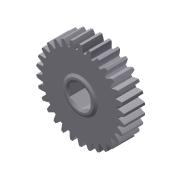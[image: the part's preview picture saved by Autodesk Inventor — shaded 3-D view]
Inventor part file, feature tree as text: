
AUTODESK INVENTOR PART (.ipt)
format: ipt  version: 2011 (Build 150239000, 239)  size: 292,352 bytes
history: native  units: mm (DEFAULTED — no unit token found)
features: sketch x5, other x4, extrude x3, plane x3, revolve x1, projected_geometry x1
ambient origin geometry x8: Origin, YZ Plane, XZ Plane, XY Plane, X Axis, Y Axis, Z Axis, Center Point
bodies: Solid1 (feature_tree)
feature tree (17):
  other  "Gear 30T 20dp 375hex"
  extrude  "Extrusion1"  Depth=9.525mm TaperAngle=0.0deg
  plane  "Work Plane1"
  plane  "Work Plane2"
  plane  "Work Plane3"
  other  "Spur Gear"
  extrude  "Extrusion2"  Depth=76.2mm TaperAngle=0.0deg
  extrude  "Extrusion3"  TaperAngle=0.0deg  [1 undecoded]
  revolve  "Revolution1"  [1 undecoded]
  sketch  "Sketch1"  dims[d0=40.64mm d1=9.525mm d2=0.0mm]
  sketch  "Sketch2"  dims[d3=38.1mm d4=76.2mm d5=0.0mm]
  other  "Srf1"
  sketch  "Sketch3"  dims[d6=0.0mm d7=1.047198mm d9=0.0mm]
  sketch  "Sketch4"  dims[d14=0.0mm d15=95.25mm d16=0.0mm]
  sketch  "Sketch5"  dims[d17=0.0mm d18=0.0mm d19=95.25mm d20=15.9004mm d21=0.635mm d22=0.0mm d23=9.525mm d24=0.635mm d25=0.0mm d26=1.143mm d27=0.889mm d28=5.070181mm d29=2.54mm d30=90.0deg]
  other  "Pitch Diameter"
  projected_geometry  "Project Cut Edges1"
note: 2 required parameter values undecoded (feature->parameter linkage not recoverable at this tier; creation-order binding heuristic only, values carry confidence <= 0.55)